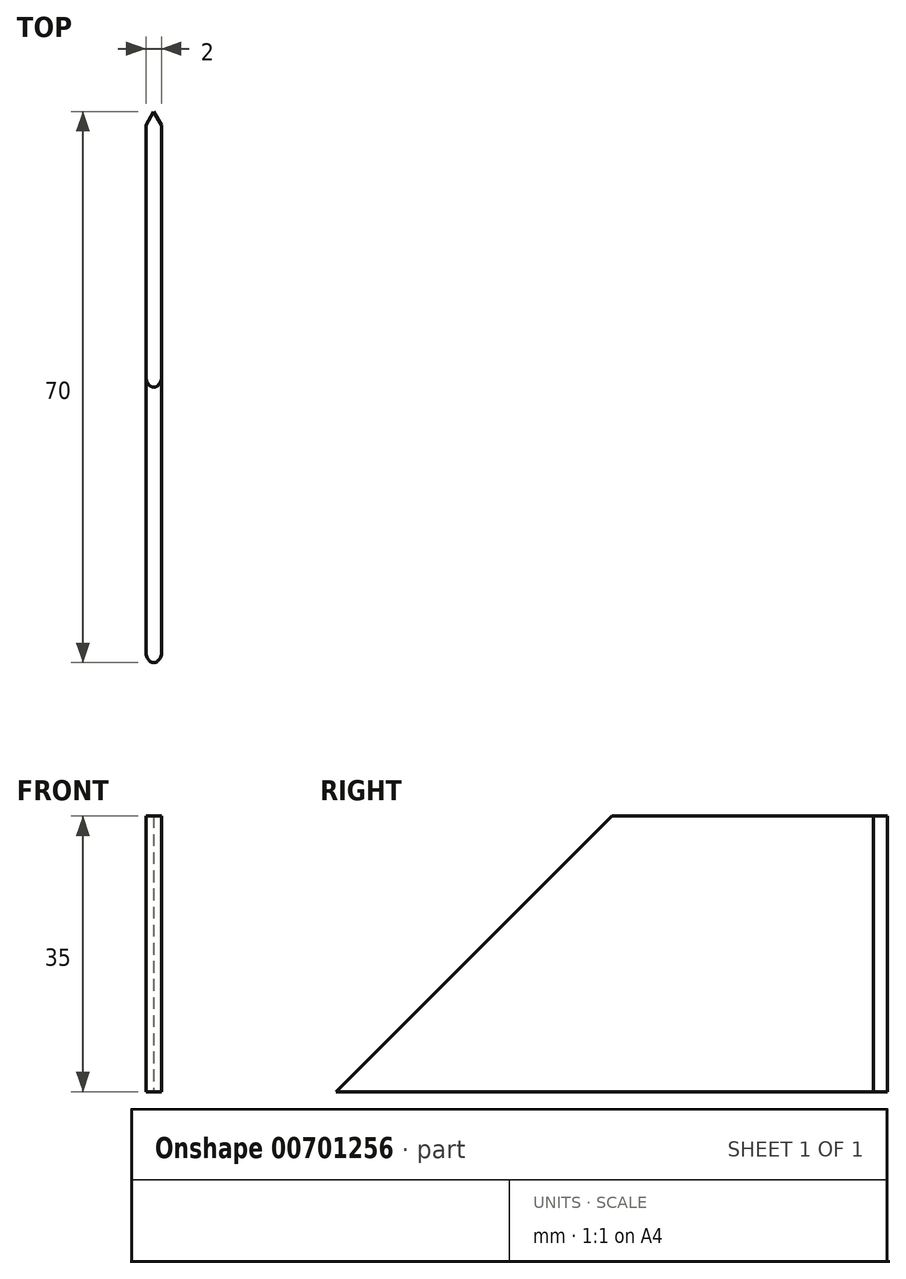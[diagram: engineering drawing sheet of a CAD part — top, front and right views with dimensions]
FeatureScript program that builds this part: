
annotation { "Feature Type Name" : "Feature", "Feature Type Description" : "" }
export const myFeature = defineFeature(function(context is Context, id is Id, definition is map)
    precondition{}
    {
        {
            var Q0;
            Q0=qCreatedBy(makeId("Right.planeOp"),FACE);
            var sketch = newSketch(context, id + "F0", { "sketchPlane" : qUnion([Q0])});
            skLineSegment(sketch, "E0", {"start": v(0, 0) * mm, "end": v(-70, 0) * mm});
            skLineSegment(sketch, "E1", {"start": v(-70, 0) * mm, "end": v(-35, 35) * mm});
            skLineSegment(sketch, "E2", {"start": v(-35, 35) * mm, "end": v(0, 35) * mm});
            skLineSegment(sketch, "E3", {"start": v(0, 35) * mm, "end": v(0, 0) * mm});
            skLineSegment(sketch, "E4.bottom", {"start": v(-70, 0) * mm, "end": v(0, 0) * mm});
            skLineSegment(sketch, "E4.top", {"start": v(-70, -5) * mm, "end": v(0, -5) * mm});
            skLineSegment(sketch, "E4.left", {"start": v(-70, 0) * mm, "end": v(-70, -5) * mm});
            skLineSegment(sketch, "E4.right", {"start": v(0, 0) * mm, "end": v(0, -5) * mm});
            skSolve(sketch);
        }
        {
            var Q0;
            Q0=makeQuery(id+"F0.imprint","IMPRINT",FACE,{"disambiguationData":[TD([[makeQuery(id+"F0.imprint","IMPRINT",EDGE,{"derivedFrom":sQuery(id+"F0.wireOp",EDGE,"E1")}),-1.0]])]});
            var Q1;
            Q1=makeQuery(id+"F0.imprint","IMPRINT",FACE,{"disambiguationData":[TD([[makeQuery(id+"F0.imprint","IMPRINT",EDGE,{"derivedFrom":sQuery(id+"F0.wireOp",EDGE,"E4.bottom")}),-1.0]])]});
            extrude(context, id + "F1", {"entities" : qUnion([Q0, Q1]), "endBound" : BoundingType.SYMMETRIC, "depth" : 2 * mm, "offsetDistance" : 25 * mm});
        }
        {
            var Q0;
            Q0=makeQuery(id+"F1.opExtrude","CAP_EDGE",EDGE,{"disambiguationData":[OSD([sQuery(id+"F0.wireOp",EDGE,"E1")])],"isStart":false});
            fillet(context, id + "F2", {"entities" : qUnion([Q0]), "radius" : 1 * mm, "tangentPropagation" : true, "allowEdgeOverflow" : false});
        }
        {
            var Q0;
            Q0=makeQuery(id+"F1.opExtrude","CAP_EDGE",EDGE,{"disambiguationData":[OSD([sQuery(id+"F0.wireOp",EDGE,"E1")])],"isStart":true});
            fillet(context, id + "F3", {"entities" : qUnion([Q0]), "radius" : 1 * mm, "tangentPropagation" : true, "allowEdgeOverflow" : false});
        }
        {
            var Q0;
            Q0=qCreatedBy(makeId("Front.planeOp"),FACE);
            var sketch = newSketch(context, id + "F4", { "sketchPlane" : qUnion([Q0])});
            skLineSegment(sketch, "E5", {"start": v(0, 0) * mm, "end": v(0, -16.5) * mm});
            skCircle(sketch, "E6", {"center": v(0, -16.5) * mm, "radius": 16.5 * mm});
            skSolve(sketch);
        }
        {
            var Q0;
            Q0=qSketchRegion(id+"F4",true);
            extrude(context, id + "F5", {"entities" : qUnion([Q0]), "operationType" : NewBodyOperationType.REMOVE, "endBound" : BoundingType.SYMMETRIC, "depth" : 150 * mm, "offsetDistance" : 25 * mm});
        }
        {
            var Q0;
            Q0=makeQuery(id+"F1.opExtrude","CAP_EDGE",EDGE,{"disambiguationData":[OSD([sQuery(id+"F0.wireOp",EDGE,"E3"),sQuery(id+"F0.wireOp",EDGE,"E4.right")])],"isStart":false});
            chamfer(context, id + "F6", {"entities" : qUnion([Q0]), "chamferType" : ChamferType.OFFSET_ANGLE, "width" : 1 * mm, "oppositeDirection" : false, "angle" : 60 * degree, "tangentPropagation" : true});
        }
        {
            var Q0;
            Q0=makeQuery(id+"F1.opExtrude","CAP_EDGE",EDGE,{"disambiguationData":[OSD([sQuery(id+"F0.wireOp",EDGE,"E3"),sQuery(id+"F0.wireOp",EDGE,"E4.right")])],"isStart":true});
            chamfer(context, id + "F7", {"entities" : qUnion([Q0]), "chamferType" : ChamferType.OFFSET_ANGLE, "width" : 1 * mm, "oppositeDirection" : true, "angle" : 60 * degree, "tangentPropagation" : true});
        }
    });
